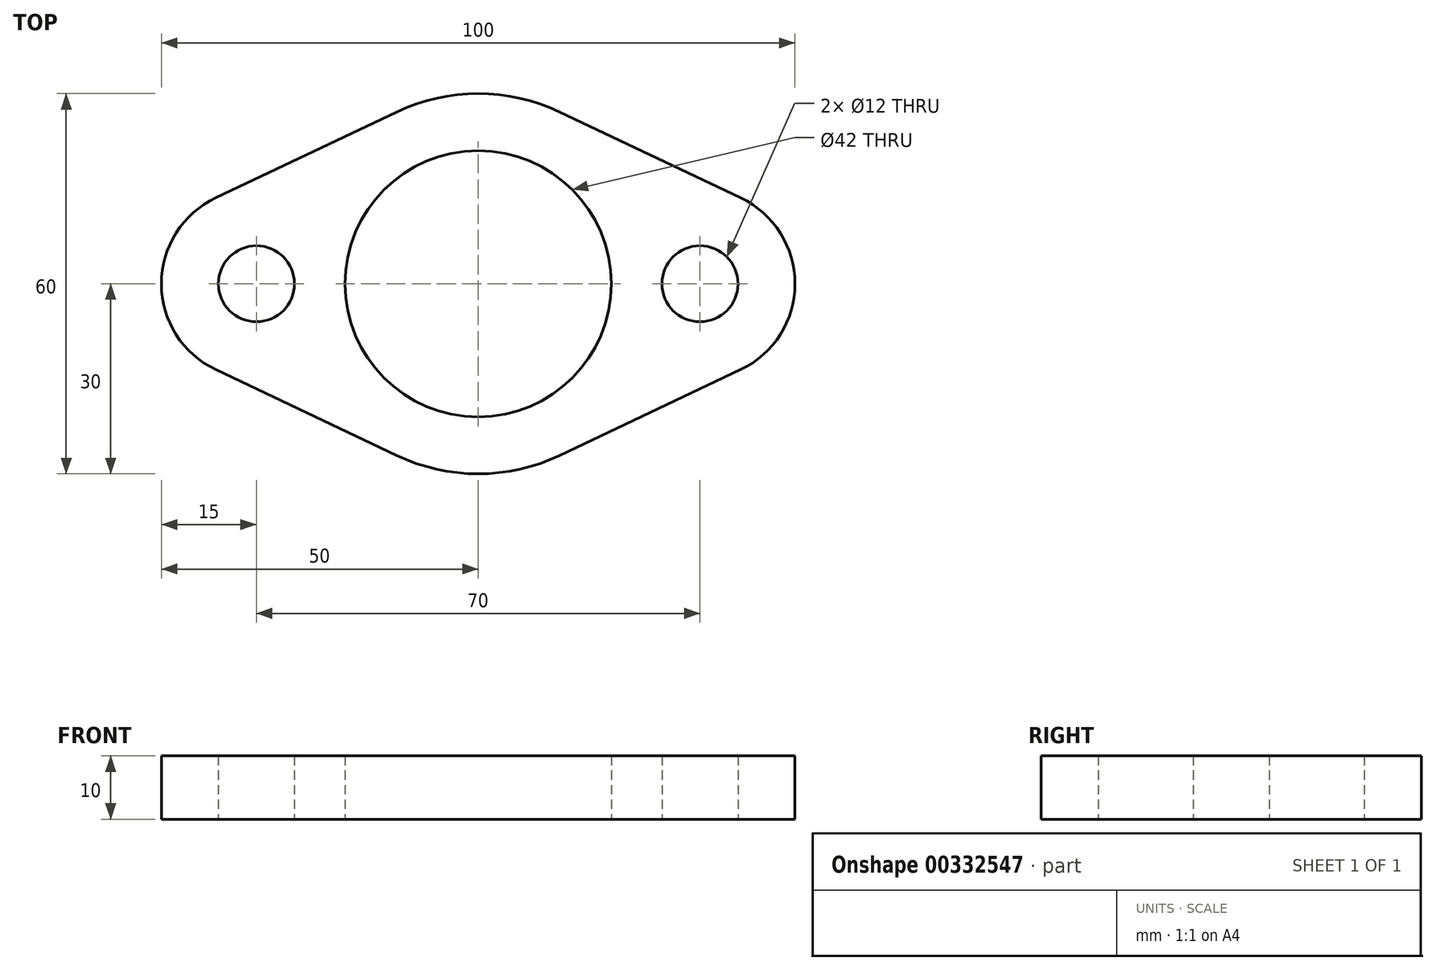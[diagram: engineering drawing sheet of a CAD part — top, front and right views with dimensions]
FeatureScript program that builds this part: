
annotation { "Feature Type Name" : "Feature", "Feature Type Description" : "" }
export const myFeature = defineFeature(function(context is Context, id is Id, definition is map)
    precondition{}
    {
        {
            var Q0;
            Q0=qCreatedBy(makeId("Top.planeOp"),FACE);
            var sketch = newSketch(context, id + "F0", { "sketchPlane" : qUnion([Q0])});
            skArc(sketch, "E0", {"start": v(-12.86, -27.1) * mm, "mid": v(0, -30) * mm, "end": v(12.86, -27.1) * mm});
            skCircle(sketch, "E1", {"center": v(0, 0) * mm, "radius": 21 * mm});
            skPoint(sketch, "E2", {"position": v(-35, 0) * mm});
            skPoint(sketch, "E3", {"position": v(35, 0) * mm});
            skCircle(sketch, "E4", {"center": v(-35, 0) * mm, "radius": 6 * mm});
            skCircle(sketch, "E5", {"center": v(35, 0) * mm, "radius": 6 * mm});
            skArc(sketch, "E6.trimOffspring", {"start": v(12.86, 27.1) * mm, "mid": v(0, 30) * mm, "end": v(-12.86, 27.1) * mm});
            skArc(sketch, "E7", {"start": v(-41.43, 13.55) * mm, "mid": v(-50, 0) * mm, "end": v(-41.43, -13.55) * mm});
            skArc(sketch, "E8", {"start": v(41.43, -13.55) * mm, "mid": v(50, 0) * mm, "end": v(41.43, 13.55) * mm});
            skLineSegment(sketch, "E9", {"start": v(-12.86, 27.1) * mm, "end": v(-41.43, 13.55) * mm});
            skLineSegment(sketch, "E10", {"start": v(12.86, 27.1) * mm, "end": v(41.43, 13.55) * mm});
            skLineSegment(sketch, "E11", {"start": v(41.43, -13.55) * mm, "end": v(12.64, -27.2) * mm});
            skLineSegment(sketch, "E12", {"start": v(-41.43, -13.55) * mm, "end": v(-12.86, -27.1) * mm});
            skPoint(sketch, "E13.orphan", {"position": v(0, -33.2) * mm});
            skSolve(sketch);
        }
        {
            var Q0;
            Q0 = qSketchRegion(id + "F0", true);
            extrude(context, id + "F1", {"entities" : qUnion([Q0]), "depth" : 10 * mm});
        }
    });
